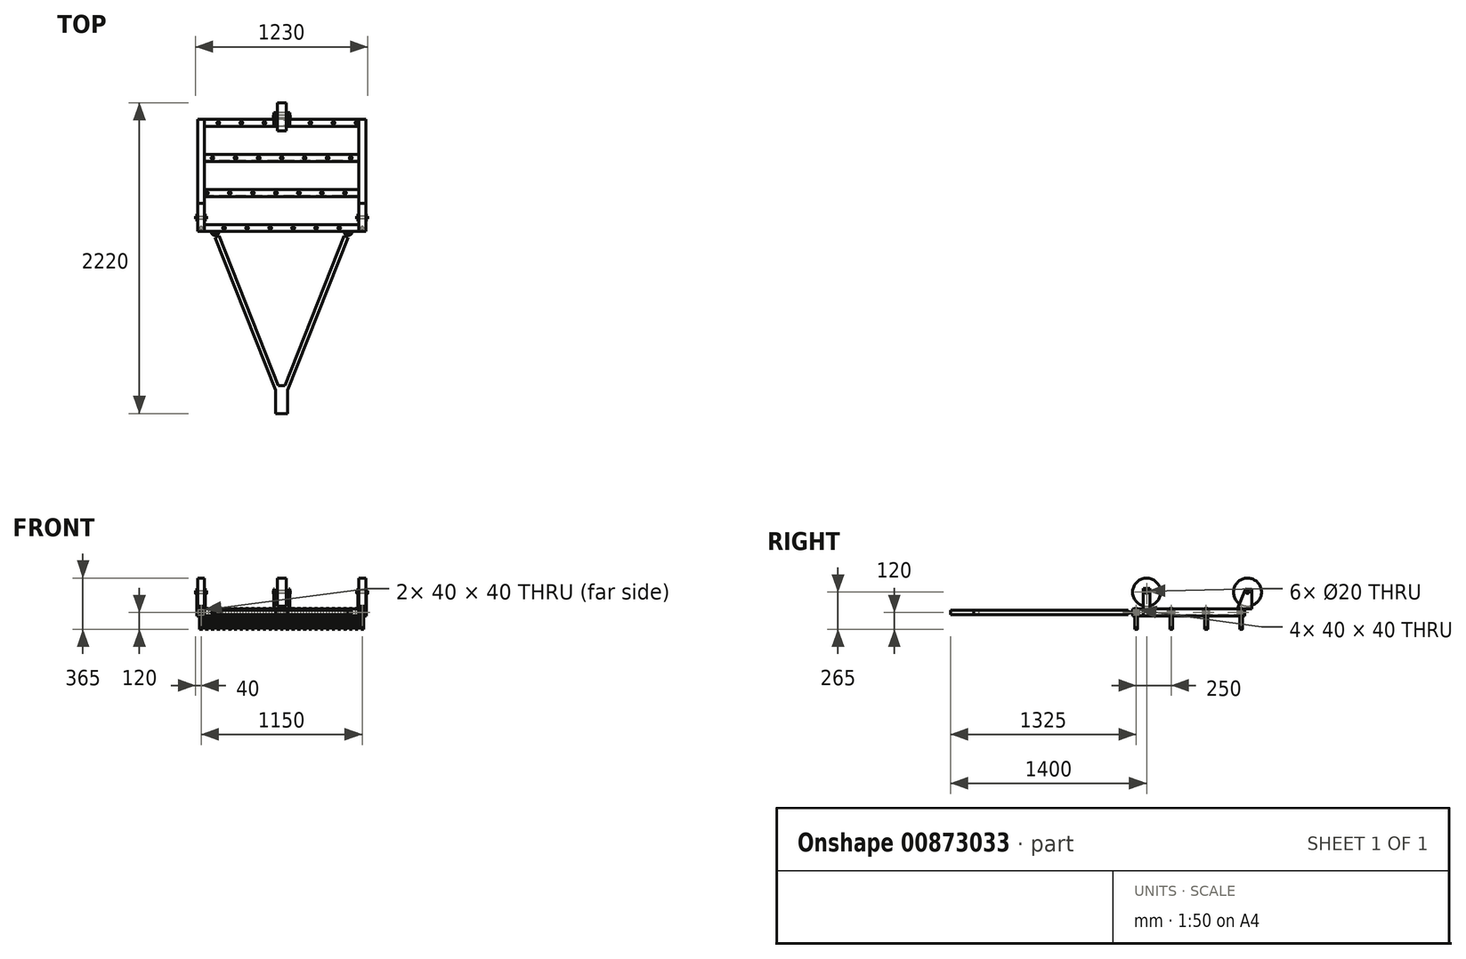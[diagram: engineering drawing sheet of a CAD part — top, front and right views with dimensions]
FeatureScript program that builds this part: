
annotation { "Feature Type Name" : "Feature", "Feature Type Description" : "" }
export const myFeature = defineFeature(function(context is Context, id is Id, definition is map)
    precondition{}
    {
        {
            assignVariable(context, id + "F0", {"name" : "Width", "anyValue" : 1200});
        }
        {
            assignVariable(context, id + "F1", {"name" : "PipeWidth", "anyValue" : 50});
        }
        {
            var Q0;
            Q0=qCreatedBy(makeId("Right.planeOp"),FACE);
            var sketch = newSketch(context, id + "F2", { "sketchPlane" : qUnion([Q0])});
            skLineSegment(sketch, "E0.bottom", {"start": v(-400, 0) * mm, "end": v(-350, 0) * mm});
            skLineSegment(sketch, "E0.top", {"start": v(-400, 50) * mm, "end": v(-350, 50) * mm});
            skLineSegment(sketch, "E0.left", {"start": v(-400, 0) * mm, "end": v(-400, 50) * mm});
            skLineSegment(sketch, "E0.right", {"start": v(-350, 0) * mm, "end": v(-350, 50) * mm});
            skLineSegment(sketch, "E1.bottom", {"start": v(-150, 0) * mm, "end": v(-100, 0) * mm});
            skLineSegment(sketch, "E1.top", {"start": v(-150, 50) * mm, "end": v(-100, 50) * mm});
            skLineSegment(sketch, "E1.left", {"start": v(-150, 0) * mm, "end": v(-150, 50) * mm});
            skLineSegment(sketch, "E1.right", {"start": v(-100, 0) * mm, "end": v(-100, 50) * mm});
            skLineSegment(sketch, "E2.bottom", {"start": v(-395, 45) * mm, "end": v(-355, 45) * mm});
            skLineSegment(sketch, "E2.top", {"start": v(-395, 5) * mm, "end": v(-355, 5) * mm});
            skLineSegment(sketch, "E2.left", {"start": v(-395, 45) * mm, "end": v(-395, 5) * mm});
            skLineSegment(sketch, "E2.right", {"start": v(-355, 45) * mm, "end": v(-355, 5) * mm});
            skLineSegment(sketch, "E3.bottom", {"start": v(-145, 45) * mm, "end": v(-105, 45) * mm});
            skLineSegment(sketch, "E3.top", {"start": v(-145, 5) * mm, "end": v(-105, 5) * mm});
            skLineSegment(sketch, "E3.left", {"start": v(-145, 45) * mm, "end": v(-145, 5) * mm});
            skLineSegment(sketch, "E3.right", {"start": v(-105, 45) * mm, "end": v(-105, 5) * mm});
            skLineSegment(sketch, "E4", {"start": v(-250, 126.44) * mm, "end": v(-250, -177.28) * mm, "construction": true});
            skLineSegment(sketch, "E5", {"start": v(-350, 17.34) * mm, "end": v(-250, 17.34) * mm, "construction": true});
            skLineSegment(sketch, "E6", {"start": v(-150, 39.41) * mm, "end": v(-250, 39.41) * mm, "construction": true});
            skLineSegment(sketch, "E7", {"start": v(0, 0) * mm, "end": v(0, 122.09) * mm, "construction": true});
            skLineSegment(sketch, "E8", {"start": v(0, 23.9) * mm, "end": v(-100, 23.9) * mm, "construction": true});
            skSolve(sketch);
        }
        {
            var Q0;
            Q0 = qSketchRegion(id + "F2", true);
            extrude(context, id + "F3", {"entities" : qUnion([Q0]), "endBound" : BoundingType.SYMMETRIC, "depth" : (getVariable(context, 'Width') - 2 * getVariable(context, 'PipeWidth')) * mm, "offsetDistance" : 25 * mm});
        }
        {
            var Q0;
            Q0=makeQuery(id+"F3.opExtrude","SWEPT_BODY",BODY,{"disambiguationData":[OSD([sQuery(id+"F2.wireOp",EDGE,"E0.bottom"),sQuery(id+"F2.wireOp",EDGE,"E0.top"),sQuery(id+"F2.wireOp",EDGE,"E0.left"),sQuery(id+"F2.wireOp",EDGE,"E0.right")])]});
            var Q1;
            Q1=makeQuery(id+"F3.opExtrude","SWEPT_BODY",BODY,{"disambiguationData":[OSD([sQuery(id+"F2.wireOp",EDGE,"E1.bottom"),sQuery(id+"F2.wireOp",EDGE,"E1.top"),sQuery(id+"F2.wireOp",EDGE,"E1.left"),sQuery(id+"F2.wireOp",EDGE,"E1.right"),sQuery(id+"F2.wireOp",EDGE,"E3.bottom"),sQuery(id+"F2.wireOp",EDGE,"E3.top"),sQuery(id+"F2.wireOp",EDGE,"E3.left"),sQuery(id+"F2.wireOp",EDGE,"E3.right")])]});
            var Q2;
            Q2=qCreatedBy(makeId("Front.planeOp"),FACE);
            mirror(context, id + "F4", {"entities" : qUnion([Q0, Q1]), "mirrorPlane" : qUnion([Q2])});
        }
        {
            var Q0;
            Q0=makeQuery(id+"F3.opExtrude","SWEPT_FACE",FACE,{"disambiguationData":[OSD([sQuery(id+"F2.wireOp",EDGE,"E0.left")])]});
            var sketch = newSketch(context, id + "F5", { "sketchPlane" : qUnion([Q0])});
            skLineSegment(sketch, "E9.bottom", {"start": v(550, 50) * mm, "end": v(600, 50) * mm});
            skLineSegment(sketch, "E9.top", {"start": v(550, 0) * mm, "end": v(600, 0) * mm});
            skLineSegment(sketch, "E9.left", {"start": v(550, 50) * mm, "end": v(550, 0) * mm});
            skLineSegment(sketch, "E9.right", {"start": v(600, 50) * mm, "end": v(600, 0) * mm});
            skLineSegment(sketch, "E10.bottom", {"start": v(555, 45) * mm, "end": v(595, 45) * mm});
            skLineSegment(sketch, "E10.top", {"start": v(555, 5) * mm, "end": v(595, 5) * mm});
            skLineSegment(sketch, "E10.left", {"start": v(555, 45) * mm, "end": v(555, 5) * mm});
            skLineSegment(sketch, "E10.right", {"start": v(595, 45) * mm, "end": v(595, 5) * mm});
            skSolve(sketch);
        }
        {
            var Q0;
            Q0 = qSketchRegion(id + "F5", true);
            var Q1;
            Q1=makeQuery(id+"F4.opPattern","COPY",FACE,{"derivedFrom":makeQuery(id+"F3.opExtrude","SWEPT_FACE",FACE,{"disambiguationData":[OSD([sQuery(id+"F2.wireOp",EDGE,"E0.left")])]}),"instanceName":"1"});
            extrude(context, id + "F6", {"entities" : qUnion([Q0]), "endBound" : BoundingType.UP_TO_SURFACE, "oppositeDirection" : true, "depth" : 25 * mm, "endBoundEntityFace" : qUnion([Q1]), "offsetDistance" : 25 * mm});
        }
        {
            var Q0;
            Q0=makeQuery(id+"F6.opExtrude","SWEPT_BODY",BODY,{"disambiguationData":[OSD([sQuery(id+"F5.wireOp",EDGE,"E9.bottom"),sQuery(id+"F5.wireOp",EDGE,"E9.top"),sQuery(id+"F5.wireOp",EDGE,"E9.left"),sQuery(id+"F5.wireOp",EDGE,"E9.right"),sQuery(id+"F5.wireOp",EDGE,"E10.bottom"),sQuery(id+"F5.wireOp",EDGE,"E10.top"),sQuery(id+"F5.wireOp",EDGE,"E10.left"),sQuery(id+"F5.wireOp",EDGE,"E10.right")])]});
            var Q1;
            Q1=qCreatedBy(makeId("Right.planeOp"),FACE);
            mirror(context, id + "F7", {"entities" : qUnion([Q0]), "mirrorPlane" : qUnion([Q1])});
        }
        {
            assignVariable(context, id + "F8", {"name" : "PinLength", "anyValue" : 150});
        }
        {
            assignVariable(context, id + "F9", {"name" : "PinPro", "anyValue" : 5});
        }
        {
            var Q0;
            Q0=makeQuery(id+"F3.opExtrude","SWEPT_FACE",FACE,{"disambiguationData":[OSD([sQuery(id+"F2.wireOp",EDGE,"E0.top")])]});
            var sketch = newSketch(context, id + "F10", { "sketchPlane" : qUnion([Q0])});
            skCircle(sketch, "E11", {"center": v(-575, -375) * mm, "radius": 10 * mm});
            skLineSegment(sketch, "E12", {"start": v(-575, -375) * mm, "end": v(-654.38, -375) * mm, "construction": true});
            skLineSegment(sketch, "E13", {"start": v(-575, -375) * mm, "end": v(-575, -302.63) * mm, "construction": true});
            skCircle(sketch, "E14.1.0.0", {"center": v(-410.71, -375) * mm, "radius": 10 * mm});
            skCircle(sketch, "E14.2.0.0", {"center": v(-246.43, -375) * mm, "radius": 10 * mm});
            skCircle(sketch, "E14.3.0.0", {"center": v(-82.14, -375) * mm, "radius": 10 * mm});
            skCircle(sketch, "E14.4.0.0", {"center": v(82.14, -375) * mm, "radius": 10 * mm});
            skCircle(sketch, "E14.5.0.0", {"center": v(246.43, -375) * mm, "radius": 10 * mm});
            skCircle(sketch, "E14.6.0.0", {"center": v(410.71, -375) * mm, "radius": 10 * mm});
            skCircle(sketch, "E14.7.0.0", {"center": v(575, -375) * mm, "radius": 10 * mm});
            skLineSegment(sketch, "E14.direction1", {"start": v(-575, -375) * mm, "end": v(-410.71, -375) * mm, "construction": true});
            skSolve(sketch);
        }
        {
            var Q0;
            Q0 = qSketchRegion(id + "F10", true);
            extrude(context, id + "F11", {"entities" : qUnion([Q0]), "depth" : (getVariable(context, 'PinPro')) * mm, "offsetDistance" : 25 * mm, "hasSecondDirection" : true, "secondDirectionOppositeDirection" : true, "secondDirectionDepth" : (getVariable(context, 'PinLength') - getVariable(context, 'PinPro')) * mm});
        }
        {
            var Q0;
            Q0=makeQuery(id+"F3.opExtrude","SWEPT_FACE",FACE,{"disambiguationData":[OSD([sQuery(id+"F2.wireOp",EDGE,"E1.top")])]});
            var sketch = newSketch(context, id + "F12", { "sketchPlane" : qUnion([Q0])});
            skCircle(sketch, "E15.0.0", {"center": v(-575, -375) * mm, "radius": 10 * mm, "construction": true});
            skLineSegment(sketch, "E16", {"start": v(-575, -375) * mm, "end": v(-575, -49.27) * mm, "construction": true});
            skCircle(sketch, "E17", {"center": v(-533.93, -125) * mm, "radius": 10 * mm});
            skLineSegment(sketch, "E18", {"start": v(-533.93, -125) * mm, "end": v(-621.5, -125) * mm, "construction": true});
            skCircle(sketch, "E19.1.0.0", {"center": v(-369.64, -125) * mm, "radius": 10 * mm});
            skCircle(sketch, "E19.2.0.0", {"center": v(-205.36, -125) * mm, "radius": 10 * mm});
            skCircle(sketch, "E19.3.0.0", {"center": v(-41.07, -125) * mm, "radius": 10 * mm});
            skCircle(sketch, "E19.4.0.0", {"center": v(123.21, -125) * mm, "radius": 10 * mm});
            skCircle(sketch, "E19.5.0.0", {"center": v(287.5, -125) * mm, "radius": 10 * mm});
            skCircle(sketch, "E19.6.0.0", {"center": v(451.79, -125) * mm, "radius": 10 * mm});
            skLineSegment(sketch, "E19.direction1", {"start": v(-533.93, -125) * mm, "end": v(-369.64, -125) * mm, "construction": true});
            skSolve(sketch);
        }
        {
            var Q0;
            Q0 = qSketchRegion(id + "F12", true);
            extrude(context, id + "F13", {"entities" : qUnion([Q0]), "depth" : (getVariable(context, 'PinPro')) * mm, "offsetDistance" : 25 * mm, "hasSecondDirection" : true, "secondDirectionOppositeDirection" : true, "secondDirectionDepth" : (getVariable(context, 'PinLength') - getVariable(context, 'PinPro')) * mm});
        }
        {
            var Q0;
            Q0=makeQuery(id+"F4.opPattern","COPY",FACE,{"derivedFrom":makeQuery(id+"F3.opExtrude","SWEPT_FACE",FACE,{"disambiguationData":[OSD([sQuery(id+"F2.wireOp",EDGE,"E1.top")])]}),"instanceName":"1"});
            var sketch = newSketch(context, id + "F14", { "sketchPlane" : qUnion([Q0])});
            skCircle(sketch, "E20.0.0", {"center": v(-575, -375) * mm, "radius": 10 * mm, "construction": true});
            skLineSegment(sketch, "E21", {"start": v(-575, -375) * mm, "end": v(-575, 246.53) * mm, "construction": true});
            skLineSegment(sketch, "E22", {"start": v(-492.86, 125) * mm, "end": v(-662.53, 125) * mm, "construction": true});
            skCircle(sketch, "E23", {"center": v(-492.86, 125) * mm, "radius": 10 * mm});
            skCircle(sketch, "E24.1.0.0", {"center": v(-328.57, 125) * mm, "radius": 10 * mm});
            skCircle(sketch, "E24.2.0.0", {"center": v(-164.29, 125) * mm, "radius": 10 * mm});
            skCircle(sketch, "E24.3.0.0", {"center": v(0, 125) * mm, "radius": 10 * mm});
            skCircle(sketch, "E24.4.0.0", {"center": v(164.29, 125) * mm, "radius": 10 * mm});
            skCircle(sketch, "E24.5.0.0", {"center": v(328.57, 125) * mm, "radius": 10 * mm});
            skCircle(sketch, "E24.6.0.0", {"center": v(492.86, 125) * mm, "radius": 10 * mm});
            skLineSegment(sketch, "E24.direction1", {"start": v(-492.86, 125) * mm, "end": v(-328.57, 125) * mm, "construction": true});
            skSolve(sketch);
        }
        {
            var Q0;
            Q0 = qSketchRegion(id + "F14", true);
            extrude(context, id + "F15", {"entities" : qUnion([Q0]), "depth" : (getVariable(context, 'PinPro')) * mm, "offsetDistance" : 25 * mm, "hasSecondDirection" : true, "secondDirectionOppositeDirection" : true, "secondDirectionDepth" : (getVariable(context, 'PinLength') - getVariable(context, 'PinPro')) * mm});
        }
        {
            var Q0;
            Q0=makeQuery(id+"F4.opPattern","COPY",FACE,{"derivedFrom":makeQuery(id+"F3.opExtrude","SWEPT_FACE",FACE,{"disambiguationData":[OSD([sQuery(id+"F2.wireOp",EDGE,"E0.top")])]}),"instanceName":"1"});
            var sketch = newSketch(context, id + "F16", { "sketchPlane" : qUnion([Q0])});
            skCircle(sketch, "E25.0", {"center": v(-575, -375) * mm, "radius": 10 * mm, "construction": true});
            skLineSegment(sketch, "E26", {"start": v(-575, -375) * mm, "end": v(-575, 476.67) * mm, "construction": true});
            skLineSegment(sketch, "E27", {"start": v(-451.79, 375) * mm, "end": v(-656.1, 375) * mm, "construction": true});
            skCircle(sketch, "E28", {"center": v(-451.79, 375) * mm, "radius": 10 * mm});
            skCircle(sketch, "E29.1.0.0", {"center": v(-287.5, 375) * mm, "radius": 10 * mm});
            skCircle(sketch, "E29.2.0.0", {"center": v(-123.21, 375) * mm, "radius": 10 * mm});
            skCircle(sketch, "E29.3.0.0", {"center": v(41.07, 375) * mm, "radius": 10 * mm});
            skCircle(sketch, "E29.4.0.0", {"center": v(205.36, 375) * mm, "radius": 10 * mm});
            skCircle(sketch, "E29.5.0.0", {"center": v(369.64, 375) * mm, "radius": 10 * mm});
            skCircle(sketch, "E29.6.0.0", {"center": v(533.93, 375) * mm, "radius": 10 * mm});
            skLineSegment(sketch, "E29.direction1", {"start": v(-451.79, 375) * mm, "end": v(-287.5, 375) * mm, "construction": true});
            skSolve(sketch);
        }
        {
            var Q0;
            Q0 = qSketchRegion(id + "F16", true);
            extrude(context, id + "F17", {"entities" : qUnion([Q0]), "depth" : (getVariable(context, 'PinPro')) * mm, "offsetDistance" : 25 * mm, "hasSecondDirection" : true, "secondDirectionOppositeDirection" : true, "secondDirectionDepth" : (getVariable(context, 'PinLength') - getVariable(context, 'PinPro')) * mm});
        }
        {
            var Q0;
            Q0=makeQuery(id+"F3.opExtrude","SWEPT_FACE",FACE,{"disambiguationData":[OSD([sQuery(id+"F2.wireOp",EDGE,"E0.top")])]});
            var Q1;
            Q1=makeQuery(id+"F3.opExtrude","SWEPT_FACE",FACE,{"disambiguationData":[OSD([sQuery(id+"F2.wireOp",EDGE,"E0.bottom")])]});
            cPlane(context, id + "F18", {"entities" : qUnion([Q0, Q1]), "cplaneType" : CPlaneType.MID_PLANE, "offset" : 25 * mm, "width" : 150 * mm, "height" : 150 * mm});
        }
        {
            var Q0;
            Q0=qCreatedBy(id+"F18.planeOp",FACE);
            var sketch = newSketch(context, id + "F19", { "sketchPlane" : qUnion([Q0])});
            skArc(sketch, "E30", {"start": v(-500, -400) * mm, "mid": v(-475, -425) * mm, "end": v(-450, -400) * mm});
            skSolve(sketch);
        }
        {
            var Q0;
            Q0=sQuery(id+"F19.wireOp",VERTEX,"E30.end");
            var Q1;
            Q1=sQuery(id+"F19.wireOp",EDGE,"E30");
            cPlane(context, id + "F20", {"entities" : qUnion([Q0, Q1]), "cplaneType" : CPlaneType.CURVE_POINT, "offset" : 25 * mm, "width" : 150 * mm, "height" : 150 * mm});
        }
        {
            var Q0;
            Q0=qCreatedBy(id+"F20.planeOp",FACE);
            var sketch = newSketch(context, id + "F21", { "sketchPlane" : qUnion([Q0])});
            skCircle(sketch, "E31", {"center": v(450, 25) * mm, "radius": 4 * mm});
            skSolve(sketch);
        }
        {
            var Q0;
            Q0=makeQuery(id+"F21.imprint","IMPRINT",FACE,{"disambiguationData":[TD([[makeQuery(id+"F21.imprint","IMPRINT",EDGE,{"derivedFrom":sQuery(id+"F21.wireOp",EDGE,"E31")}),1.0]])]});
            var Q1;
            Q1=sQuery(id+"F19.wireOp",EDGE,"E30");
            sweep(context, id + "F22", {"profiles" : qUnion([Q0]), "path" : qUnion([Q1])});
        }
        {
            var Q0;
            Q0=makeQuery(id+"F22.opSweep","SWEPT_BODY",BODY,{"disambiguationData":[OSD([sQuery(id+"F19.wireOp",EDGE,"E30"),sQuery(id+"F21.wireOp",EDGE,"E31")])]});
            var Q1;
            Q1=qCreatedBy(makeId("Right.planeOp"),FACE);
            mirror(context, id + "F23", {"entities" : qUnion([Q0]), "mirrorPlane" : qUnion([Q1])});
        }
        {
            var Q0;
            Q0=qCreatedBy(id+"F18.planeOp",FACE);
            var sketch = newSketch(context, id + "F24", { "sketchPlane" : qUnion([Q0])});
            skLineSegment(sketch, "E32", {"start": v(-474.23, -442.71) * mm, "end": v(-42.5, -1533.39) * mm});
            skLineSegment(sketch, "E33", {"start": v(-42.5, -1533.39) * mm, "end": v(-14.6, -1522.35) * mm});
            skLineSegment(sketch, "E34", {"start": v(-14.6, -1522.35) * mm, "end": v(-446.33, -431.67) * mm});
            skLineSegment(sketch, "E35", {"start": v(-446.33, -431.67) * mm, "end": v(-474.23, -442.71) * mm});
            skLineSegment(sketch, "E36", {"start": v(474.23, -442.71) * mm, "end": v(42.5, -1533.39) * mm});
            skLineSegment(sketch, "E37", {"start": v(42.5, -1533.39) * mm, "end": v(14.6, -1522.35) * mm});
            skLineSegment(sketch, "E38", {"start": v(14.6, -1522.35) * mm, "end": v(446.33, -431.67) * mm});
            skLineSegment(sketch, "E39", {"start": v(446.33, -431.67) * mm, "end": v(474.23, -442.71) * mm});
            skLineSegment(sketch, "E40", {"start": v(0, 0) * mm, "end": v(0, -1779.1) * mm, "construction": true});
            skLineSegment(sketch, "E41", {"start": v(0, -1600) * mm, "end": v(-475, -400) * mm, "construction": true});
            skLineSegment(sketch, "E42", {"start": v(0, -1600) * mm, "end": v(475, -400) * mm, "construction": true});
            skArc(sketch, "E43", {"start": v(446, -400) * mm, "mid": v(475, -429) * mm, "end": v(504, -400) * mm, "construction": true});
            skArc(sketch, "E44", {"start": v(-504, -400) * mm, "mid": v(-475, -429) * mm, "end": v(-446, -400) * mm, "construction": true});
            skLineSegment(sketch, "E45.bottom", {"start": v(42.5, -1700) * mm, "end": v(-42.5, -1700) * mm});
            skLineSegment(sketch, "E45.top", {"start": v(42.5, -1500) * mm, "end": v(-42.5, -1500) * mm});
            skLineSegment(sketch, "E45.left", {"start": v(42.5, -1700) * mm, "end": v(42.5, -1500) * mm});
            skLineSegment(sketch, "E45.right", {"start": v(-42.5, -1700) * mm, "end": v(-42.5, -1500) * mm});
            skPoint(sketch, "E45.middle", {"position": v(0, -1600) * mm});
            skSolve(sketch);
        }
        {
            var Q0;
            Q0 = qSketchRegion(id + "F24", true);
            extrude(context, id + "F25", {"entities" : qUnion([Q0]), "endBound" : BoundingType.SYMMETRIC, "depth" : 30 * mm, "offsetDistance" : 25 * mm});
        }
        {
            var Q0;
            Q0=makeQuery(id+"F6.opExtrude","SWEPT_FACE",FACE,{"disambiguationData":[OSD([sQuery(id+"F5.wireOp",EDGE,"E9.right")])]});
            var Q1;
            Q1=makeQuery(id+"F6.opExtrude","SWEPT_FACE",FACE,{"disambiguationData":[OSD([sQuery(id+"F5.wireOp",EDGE,"E9.left")])]});
            cPlane(context, id + "F26", {"entities" : qUnion([Q0, Q1]), "cplaneType" : CPlaneType.MID_PLANE, "offset" : 25 * mm, "width" : 150 * mm, "height" : 150 * mm});
        }
        {
            var Q0;
            Q0=qCreatedBy(id+"F26.planeOp",FACE);
            var sketch = newSketch(context, id + "F27", { "sketchPlane" : qUnion([Q0])});
            skCircle(sketch, "E46", {"center": v(-300, 170) * mm, "radius": 100 * mm});
            skCircle(sketch, "E47", {"center": v(-300, 170) * mm, "radius": 10 * mm});
            skSolve(sketch);
        }
        {
            var Q0;
            Q0 = qSketchRegion(id + "F27", true);
            extrude(context, id + "F28", {"entities" : qUnion([Q0]), "endBound" : BoundingType.SYMMETRIC, "depth" : 50 * mm, "offsetDistance" : 25 * mm});
        }
        {
            var Q0;
            Q0=makeQuery(id+"F6.opExtrude","SWEPT_FACE",FACE,{"disambiguationData":[OSD([sQuery(id+"F5.wireOp",EDGE,"E9.right")])]});
            var sketch = newSketch(context, id + "F29", { "sketchPlane" : qUnion([Q0])});
            skCircle(sketch, "E48.0", {"center": v(-300, 170) * mm, "radius": 10 * mm});
            skLineSegment(sketch, "E49.bottom", {"start": v(-275, 0) * mm, "end": v(-325, 0) * mm});
            skLineSegment(sketch, "E49.top", {"start": v(-275, 195) * mm, "end": v(-325, 195) * mm});
            skLineSegment(sketch, "E49.left", {"start": v(-275, 0) * mm, "end": v(-275, 195) * mm});
            skLineSegment(sketch, "E49.right", {"start": v(-325, 0) * mm, "end": v(-325, 195) * mm});
            skPoint(sketch, "E49.middle", {"position": v(-300, 97.5) * mm});
            skSolve(sketch);
        }
        {
            var Q0;
            Q0 = qSketchRegion(id + "F29", true);
            extrude(context, id + "F30", {"entities" : qUnion([Q0]), "depth" : 5 * mm, "offsetDistance" : 25 * mm});
        }
        {
            var Q0;
            Q0=makeQuery(id+"F30.opExtrude","SWEPT_BODY",BODY,{"disambiguationData":[OSD([sQuery(id+"F29.wireOp",EDGE,"E48.0"),sQuery(id+"F29.wireOp",EDGE,"E49.bottom"),sQuery(id+"F29.wireOp",EDGE,"E49.top"),sQuery(id+"F29.wireOp",EDGE,"E49.left"),sQuery(id+"F29.wireOp",EDGE,"E49.right")])]});
            var Q1;
            Q1=qCreatedBy(id+"F26.planeOp",FACE);
            mirror(context, id + "F31", {"entities" : qUnion([Q0]), "mirrorPlane" : qUnion([Q1])});
        }
        {
            var Q0;
            Q0=makeQuery(id+"F30.opExtrude","CAP_FACE",FACE,{"disambiguationData":[OSD([sQuery(id+"F29.wireOp",EDGE,"E48.0"),sQuery(id+"F29.wireOp",EDGE,"E49.bottom"),sQuery(id+"F29.wireOp",EDGE,"E49.top"),sQuery(id+"F29.wireOp",EDGE,"E49.left"),sQuery(id+"F29.wireOp",EDGE,"E49.right")])],"isStart":false});
            var sketch = newSketch(context, id + "F32", { "sketchPlane" : qUnion([Q0])});
            skCircle(sketch, "E50.0", {"center": v(-300, 170) * mm, "radius": 10 * mm});
            skSolve(sketch);
        }
        {
            var Q0;
            Q0 = qSketchRegion(id + "F32", true);
            extrude(context, id + "F33", {"entities" : qUnion([Q0]), "depth" : 10 * mm, "offsetDistance" : 25 * mm, "hasSecondDirection" : true, "secondDirectionOppositeDirection" : true, "secondDirectionDepth" : (5 + 50 + 5 + 10) * mm});
        }
        {
            var Q0;
            Q0=makeQuery(id+"F31.opPattern","COPY",BODY,{"derivedFrom":makeQuery(id+"F30.opExtrude","SWEPT_BODY",BODY,{"disambiguationData":[OSD([sQuery(id+"F29.wireOp",EDGE,"E48.0"),sQuery(id+"F29.wireOp",EDGE,"E49.bottom"),sQuery(id+"F29.wireOp",EDGE,"E49.top"),sQuery(id+"F29.wireOp",EDGE,"E49.left"),sQuery(id+"F29.wireOp",EDGE,"E49.right")])]}),"instanceName":"1"});
            var Q1;
            Q1=makeQuery(id+"F30.opExtrude","SWEPT_BODY",BODY,{"disambiguationData":[OSD([sQuery(id+"F29.wireOp",EDGE,"E48.0"),sQuery(id+"F29.wireOp",EDGE,"E49.bottom"),sQuery(id+"F29.wireOp",EDGE,"E49.top"),sQuery(id+"F29.wireOp",EDGE,"E49.left"),sQuery(id+"F29.wireOp",EDGE,"E49.right")])]});
            var Q2;
            Q2=makeQuery(id+"F33.opExtrude","SWEPT_BODY",BODY,{"disambiguationData":[OSD([sQuery(id+"F32.wireOp",EDGE,"E50.0")])]});
            var Q3;
            Q3=makeQuery(id+"F28.opExtrude","SWEPT_BODY",BODY,{"disambiguationData":[OSD([sQuery(id+"F27.wireOp",EDGE,"E46"),sQuery(id+"F27.wireOp",EDGE,"E47")])]});
            var Q4;
            Q4=qCreatedBy(makeId("Right.planeOp"),FACE);
            mirror(context, id + "F34", {"entities" : qUnion([Q0, Q1, Q2, Q3]), "mirrorPlane" : qUnion([Q4])});
        }
        {
            var Q0;
            Q0=qCreatedBy(makeId("Right.planeOp"),FACE);
            var sketch = newSketch(context, id + "F35", { "sketchPlane" : qUnion([Q0])});
            skCircle(sketch, "E51", {"center": v(420, 170) * mm, "radius": 100 * mm});
            skSolve(sketch);
        }
        {
            var Q0;
            Q0 = qSketchRegion(id + "F35", true);
            extrude(context, id + "F36", {"entities" : qUnion([Q0]), "endBound" : BoundingType.SYMMETRIC, "depth" : 63 * mm, "offsetDistance" : 25 * mm});
        }
        {
            var Q0;
            Q0=makeQuery(id+"F4.opPattern","COPY",FACE,{"derivedFrom":makeQuery(id+"F3.opExtrude","SWEPT_FACE",FACE,{"disambiguationData":[OSD([sQuery(id+"F2.wireOp",EDGE,"E0.top")])]}),"instanceName":"1"});
            var sketch = newSketch(context, id + "F37", { "sketchPlane" : qUnion([Q0])});
            skLineSegment(sketch, "E52.bottom", {"start": v(57.5, 350) * mm, "end": v(-57.5, 350) * mm});
            skLineSegment(sketch, "E52.top", {"start": v(57.5, 450) * mm, "end": v(-57.5, 450) * mm});
            skLineSegment(sketch, "E52.left", {"start": v(57.5, 350) * mm, "end": v(57.5, 450) * mm});
            skLineSegment(sketch, "E52.right", {"start": v(-57.5, 350) * mm, "end": v(-57.5, 450) * mm});
            skPoint(sketch, "E52.middle", {"position": v(0, 400) * mm});
            skSolve(sketch);
        }
        {
            var Q0;
            Q0 = qSketchRegion(id + "F37", true);
            extrude(context, id + "F38", {"entities" : qUnion([Q0]), "depth" : 5 * mm, "offsetDistance" : 25 * mm});
        }
        {
            var Q0;
            Q0=makeQuery(id+"F38.opExtrude","SWEPT_FACE",FACE,{"disambiguationData":[OSD([sQuery(id+"F37.wireOp",EDGE,"E52.left")])]});
            var sketch = newSketch(context, id + "F39", { "sketchPlane" : qUnion([Q0])});
            skCircle(sketch, "E53.0.0", {"center": v(420, 170) * mm, "radius": 100 * mm, "construction": true});
            skLineSegment(sketch, "E54", {"start": v(350, 55) * mm, "end": v(406.06, 193.42) * mm});
            skLineSegment(sketch, "E55", {"start": v(406.06, 193.42) * mm, "end": v(450, 190.65) * mm});
            skLineSegment(sketch, "E56", {"start": v(450, 190.65) * mm, "end": v(450, 55) * mm});
            skLineSegment(sketch, "E57", {"start": v(450, 55) * mm, "end": v(350, 55) * mm});
            skSolve(sketch);
        }
        {
            var Q0;
            Q0 = qSketchRegion(id + "F39", true);
            extrude(context, id + "F40", {"entities" : qUnion([Q0]), "oppositeDirection" : true, "depth" : 5 * mm, "offsetDistance" : 25 * mm});
        }
        {
            var Q0;
            Q0=makeQuery(id+"F40.opExtrude","SWEPT_BODY",BODY,{"disambiguationData":[OSD([sQuery(id+"F39.wireOp",EDGE,"E54"),sQuery(id+"F39.wireOp",EDGE,"E55"),sQuery(id+"F39.wireOp",EDGE,"E56"),sQuery(id+"F39.wireOp",EDGE,"E57")])]});
            var Q1;
            Q1=qCreatedBy(makeId("Right.planeOp"),FACE);
            mirror(context, id + "F41", {"operationType" : NewBodyOperationType.ADD, "entities" : qUnion([Q0]), "mirrorPlane" : qUnion([Q1])});
        }
        {
            var Q0;
            Q0=makeQuery(id+"F36.opExtrude","CAP_FACE",FACE,{"disambiguationData":[OSD([sQuery(id+"F35.wireOp",EDGE,"E51")])],"isStart":false});
            var sketch = newSketch(context, id + "F42", { "sketchPlane" : qUnion([Q0])});
            skCircle(sketch, "E58.0.0", {"center": v(420, 170) * mm, "radius": 100 * mm, "construction": true});
            skCircle(sketch, "E59", {"center": v(420, 170) * mm, "radius": 10 * mm});
            skSolve(sketch);
        }
        {
            var Q0;
            Q0 = qSketchRegion(id + "F42", true);
            extrude(context, id + "F43", {"entities" : qUnion([Q0]), "depth" : 30 * mm, "offsetDistance" : 25 * mm, "hasSecondDirection" : true, "secondDirectionOppositeDirection" : true, "secondDirectionDepth" : 92 * mm});
        }
    });
